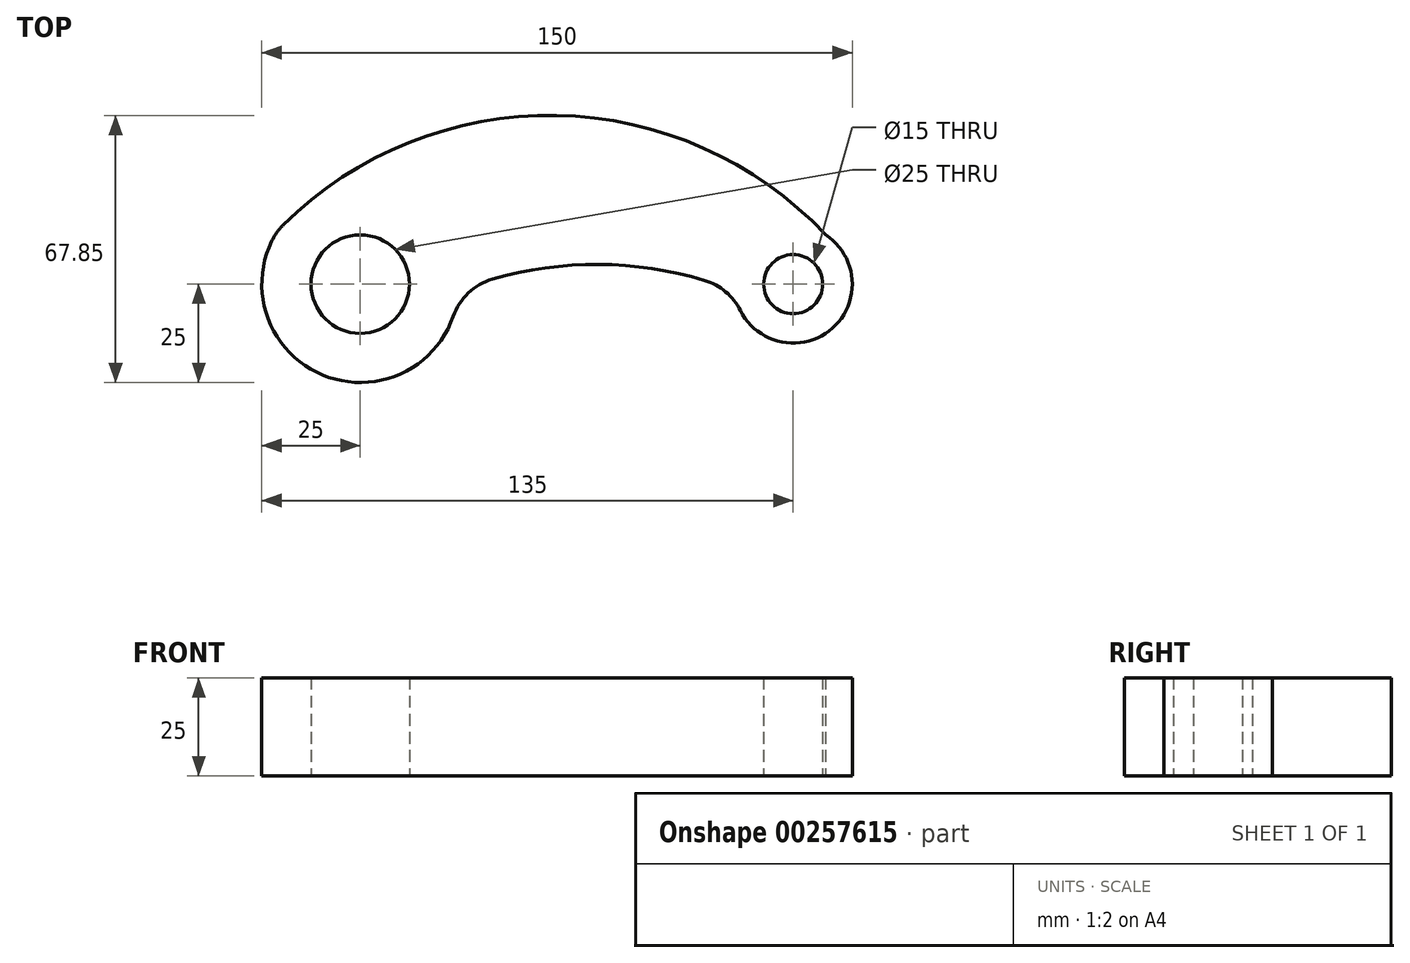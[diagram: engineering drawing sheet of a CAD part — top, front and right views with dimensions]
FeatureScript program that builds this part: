
annotation { "Feature Type Name" : "Feature", "Feature Type Description" : "" }
export const myFeature = defineFeature(function(context is Context, id is Id, definition is map)
    precondition{}
    {
        {
            var Q0;
            Q0=qCreatedBy(makeId("Top.planeOp"),FACE);
            var sketch = newSketch(context, id + "F0", { "sketchPlane" : qUnion([Q0])});
            skArc(sketch, "E0", {"start": v(-82.49, 100.92) * mm, "mid": v(-69.59, 66.91) * mm, "end": v(-36.39, 81.78) * mm});
            skArc(sketch, "E1", {"start": v(36.59, 83.29) * mm, "mid": v(60.35, 79.15) * mm, "end": v(57.34, 103.08) * mm});
            skArc(sketch, "E2", {"start": v(56.41, 76.44) * mm, "mid": v(55.6, 77.03) * mm, "end": v(54.78, 77.62) * mm});
            skArc(sketch, "E3", {"start": v(61.77, 99.3) * mm, "mid": v(59.58, 101.23) * mm, "end": v(57.34, 103.08) * mm});
            skPoint(sketch, "E3.first.point", {"position": v(-47.96, 111.9) * mm});
            skPoint(sketch, "E3.second.point", {"position": v(57.34, 103.08) * mm});
            skPoint(sketch, "E3.third.point", {"position": v(0, -70.2) * mm});
            skArc(sketch, "E4", {"start": v(-66.57, 67.78) * mm, "mid": v(-66.65, 66.85) * mm, "end": v(-66.72, 65.92) * mm});
            skArc(sketch, "E5.trimOffspring", {"start": v(55.2, 75.93) * mm, "mid": v(55, 76.78) * mm, "end": v(54.78, 77.62) * mm});
            skArc(sketch, "E6", {"start": v(63.6, 96.33) * mm, "mid": v(-6.03, 132.67) * mm, "end": v(-79.54, 105.03) * mm});
            skPoint(sketch, "E6.first.point", {"position": v(-81, 103.55) * mm});
            skPoint(sketch, "E6.second.point", {"position": v(63.6, 96.33) * mm});
            skPoint(sketch, "E6.third.point", {"position": v(18.71, -54.63) * mm});
            skPoint(sketch, "E7.orphan", {"position": v(-60, 0) * mm});
            skPoint(sketch, "E8.orphan", {"position": v(50, 0) * mm});
            skArc(sketch, "E9.trimOffspring", {"start": v(-66.57, 67.78) * mm, "mid": v(-67.3, 67.05) * mm, "end": v(-68.02, 66.32) * mm});
            skArc(sketch, "E10.trimOffspring", {"start": v(27.52, 90.93) * mm, "mid": v(0.59, 95) * mm, "end": v(-26.39, 91.26) * mm});
            skArc(sketch, "E11.filletArc", {"start": v(-26.39, 91.26) * mm, "mid": v(-32.54, 87.74) * mm, "end": v(-36.39, 81.78) * mm});
            skArc(sketch, "E12.filletArc", {"start": v(36.59, 83.29) * mm, "mid": v(32.84, 88.04) * mm, "end": v(27.52, 90.93) * mm});
            skCircle(sketch, "E13", {"center": v(-60, 90) * mm, "radius": 12.5 * mm});
            skCircle(sketch, "E14", {"center": v(50, 90) * mm, "radius": 7.5 * mm});
            skArc(sketch, "E15.filletArc", {"start": v(-79.54, 105.03) * mm, "mid": v(-81.2, 103.1) * mm, "end": v(-82.49, 100.92) * mm});
            skSolve(sketch);
        }
        {
            var Q0;
            Q0 = qSketchRegion(id + "F0", true);
            extrude(context, id + "F1", {"entities" : qUnion([Q0]), "depth" : 25 * mm});
        }
    });
